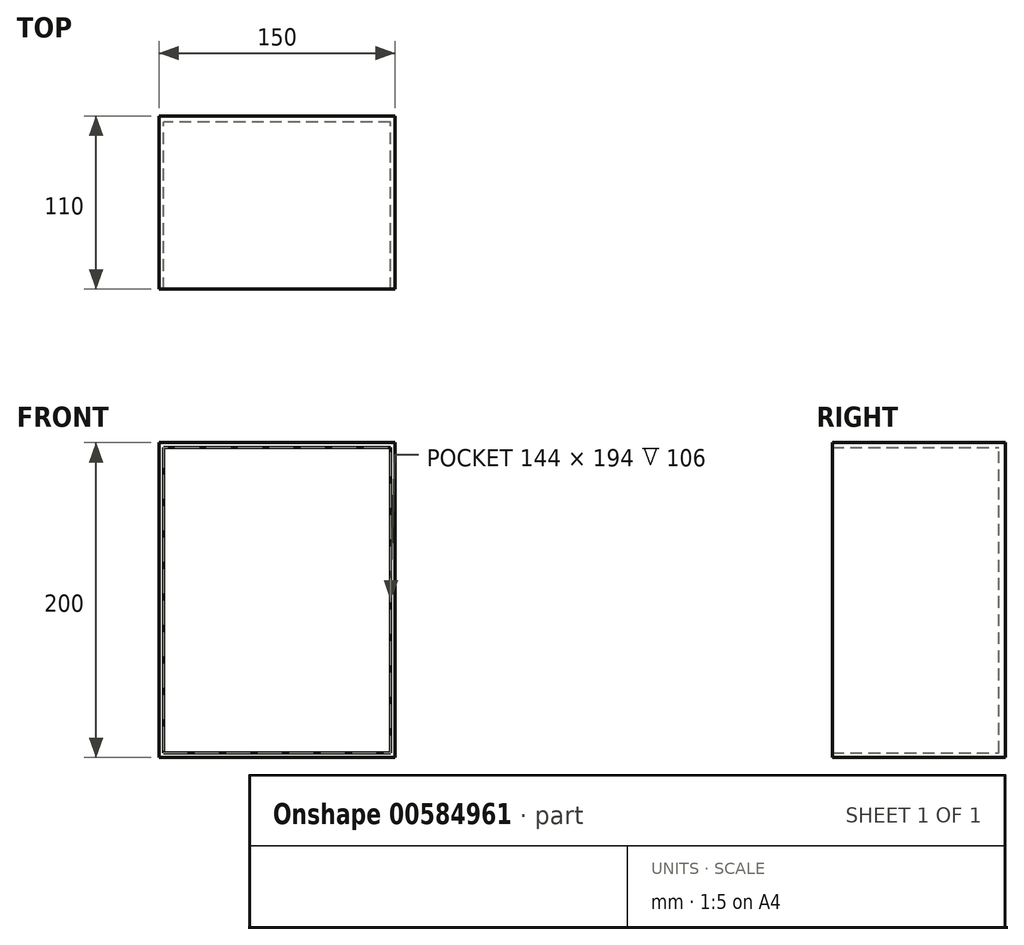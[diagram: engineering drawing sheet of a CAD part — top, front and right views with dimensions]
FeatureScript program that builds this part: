
annotation { "Feature Type Name" : "Feature", "Feature Type Description" : "" }
export const myFeature = defineFeature(function(context is Context, id is Id, definition is map)
    precondition{}
    {
        {
            var Q0;
            Q0=qCreatedBy(makeId("Front.planeOp"),FACE);
            var sketch = newSketch(context, id + "F0", { "sketchPlane" : qUnion([Q0])});
            skLineSegment(sketch, "E0.bottom", {"start": v(-75, -91.6) * mm, "end": v(75, -91.6) * mm});
            skLineSegment(sketch, "E0.top", {"start": v(-75, 108.4) * mm, "end": v(75, 108.4) * mm});
            skLineSegment(sketch, "E0.left", {"start": v(-75, -91.6) * mm, "end": v(-75, 108.4) * mm});
            skLineSegment(sketch, "E0.right", {"start": v(75, -91.6) * mm, "end": v(75, 108.4) * mm});
            skPoint(sketch, "E0.middle", {"position": v(0, 8.4) * mm});
            skLineSegment(sketch, "E1.bottom", {"start": v(72, -88.6) * mm, "end": v(-72, -88.6) * mm});
            skLineSegment(sketch, "E1.top", {"start": v(72, 105.4) * mm, "end": v(-72, 105.4) * mm});
            skLineSegment(sketch, "E1.left", {"start": v(72, -88.6) * mm, "end": v(72, 105.4) * mm});
            skLineSegment(sketch, "E1.right", {"start": v(-72, -88.6) * mm, "end": v(-72, 105.4) * mm});
            skSolve(sketch);
        }
        {
            var Q0;
            Q0=makeQuery(id+"F0.imprint","IMPRINT",FACE,{"disambiguationData":[TD([[makeQuery(id+"F0.imprint","IMPRINT",EDGE,{"derivedFrom":sQuery(id+"F0.wireOp",EDGE,"E0.bottom")}),1.0]])]});
            extrude(context, id + "F1", {"entities" : qUnion([Q0]), "depth" : 110 * mm, "offsetDistance" : 25 * mm});
        }
        {
            var Q0;
            Q0=makeQuery(id+"F0.imprint","IMPRINT",FACE,{"disambiguationData":[TD([[makeQuery(id+"F0.imprint","IMPRINT",EDGE,{"derivedFrom":sQuery(id+"F0.wireOp",EDGE,"E1.bottom")}),-1.0]])]});
            extrude(context, id + "F2", {"entities" : qUnion([Q0]), "operationType" : NewBodyOperationType.ADD, "depth" : 4 * mm, "offsetDistance" : 25 * mm});
        }
    });
